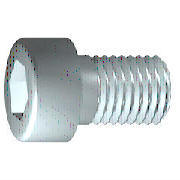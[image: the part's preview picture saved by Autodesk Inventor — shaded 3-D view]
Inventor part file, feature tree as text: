
AUTODESK INVENTOR PART (.ipt)
format: ipt  version: 2021 (Build 250183000, 183)  size: 195,072 bytes
history: native  units: mm (DEFAULTED — no unit token found)
features: sketch x2, extrude x1, plane x1, fillet x1
ambient origin geometry x7: Origin, YZ Plane, XY Plane, X Axis, Y Axis, Z Axis, Center Point
bodies: Solid1 (feature_tree), Body (feature_tree)
feature tree (5):
  extrude  "Slot"  Depth=2.5mm
  plane  "Work Plane1"
  fillet  "Fillet2"  Radius=2.5mm
  sketch  "Sketch1"  dims[d1=6.875mm d2=0.276153mm d3=2.5mm]
  sketch  "Sketch2"  dims[d4=1.1mm d5=60.0deg d6=2.5mm d7=2.5mm d8=2.309401mm d9=4.5mm d10=90.0deg d11=10.0mm d12=0.0mm d13=6.875mm d14=0.0mm d15=0.276052mm d16=0.276053mm d17=0.25mm d19=0.0mm d26=8.0mm d27=45.0deg d28=0.0mm d29=0.0mm d30=0.1mm]
